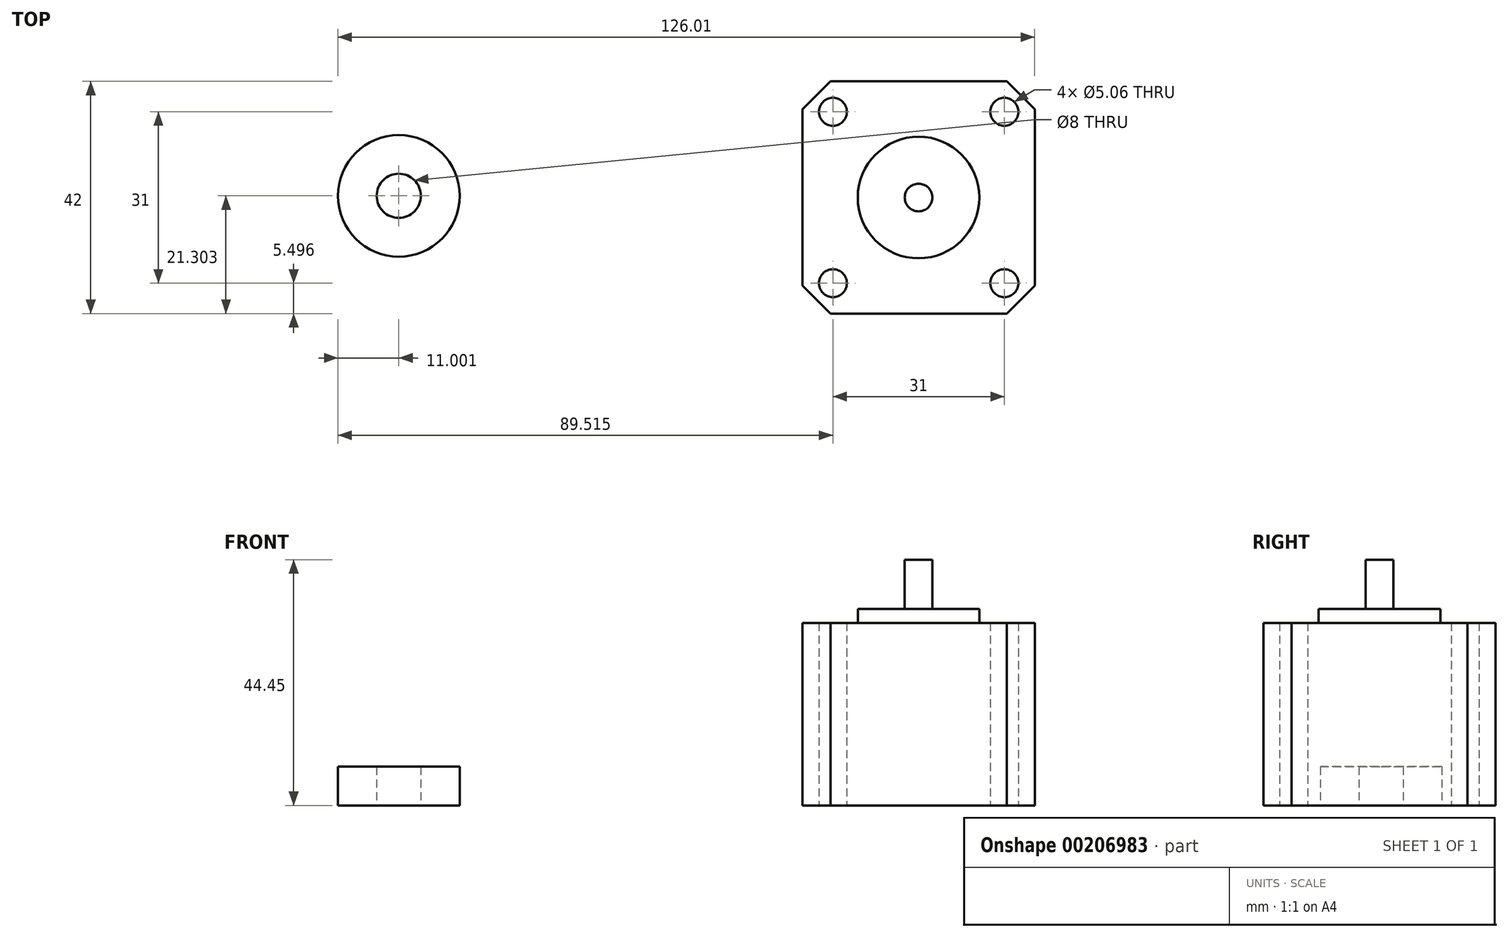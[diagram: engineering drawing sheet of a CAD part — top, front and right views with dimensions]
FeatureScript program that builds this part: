
annotation { "Feature Type Name" : "Feature", "Feature Type Description" : "" }
export const myFeature = defineFeature(function(context is Context, id is Id, definition is map)
    precondition{}
    {
        {
            var Q0;
            Q0=qCreatedBy(makeId("Top.planeOp"),FACE);
            var sketch = newSketch(context, id + "F0", { "sketchPlane" : qUnion([Q0])});
            skCircle(sketch, "E0", {"center": v(-49.86, 22.61) * mm, "radius": 11 * mm});
            skCircle(sketch, "E1", {"center": v(-49.86, 22.61) * mm, "radius": 4 * mm});
            skSolve(sketch);
        }
        {
            var Q0;
            Q0 = qSketchRegion(id + "F0", true);
            extrude(context, id + "F1", {"entities" : qUnion([Q0]), "depth" : 7 * mm});
        }
        {
            var Q0;
            Q0=qCreatedBy(makeId("Top.planeOp"),FACE);
            var sketch = newSketch(context, id + "F2", { "sketchPlane" : qUnion([Q0])});
            skLineSegment(sketch, "E2.bottom", {"start": v(23.15, 43.3) * mm, "end": v(65.15, 43.3) * mm});
            skLineSegment(sketch, "E2.top", {"start": v(23.15, 1.3) * mm, "end": v(65.15, 1.3) * mm});
            skLineSegment(sketch, "E2.left", {"start": v(23.15, 43.3) * mm, "end": v(23.15, 1.3) * mm});
            skLineSegment(sketch, "E2.right", {"start": v(65.15, 43.3) * mm, "end": v(65.15, 1.3) * mm});
            skCircle(sketch, "E3", {"center": v(44.15, 22.3) * mm, "radius": 11 * mm});
            skPoint(sketch, "E3.centerSnap0", {"position": v(23.15, 22.3) * mm});
            skPoint(sketch, "E3.centerSnap1", {"position": v(44.15, 43.3) * mm});
            skCircle(sketch, "E4", {"center": v(44.15, 22.3) * mm, "radius": 2.5 * mm});
            skCircle(sketch, "E5", {"center": v(28.65, 37.8) * mm, "radius": 2.53 * mm});
            skCircle(sketch, "E6", {"center": v(28.65, 6.8) * mm, "radius": 2.53 * mm});
            skCircle(sketch, "E7", {"center": v(59.65, 6.8) * mm, "radius": 2.53 * mm});
            skCircle(sketch, "E8", {"center": v(59.65, 37.8) * mm, "radius": 2.53 * mm});
            skLineSegment(sketch, "E9.bottom", {"start": v(28.65, 37.8) * mm, "end": v(59.65, 37.8) * mm, "construction": true});
            skLineSegment(sketch, "E9.top", {"start": v(28.65, 6.8) * mm, "end": v(59.65, 6.8) * mm, "construction": true});
            skLineSegment(sketch, "E9.left", {"start": v(28.65, 37.8) * mm, "end": v(28.65, 6.8) * mm, "construction": true});
            skLineSegment(sketch, "E9.right", {"start": v(59.65, 37.8) * mm, "end": v(59.65, 6.8) * mm, "construction": true});
            skLineSegment(sketch, "E10", {"start": v(28.65, 37.8) * mm, "end": v(28.65, 43.3) * mm, "construction": true});
            skLineSegment(sketch, "E11", {"start": v(28.65, 37.8) * mm, "end": v(23.15, 37.8) * mm, "construction": true});
            skLineSegment(sketch, "E12", {"start": v(59.65, 6.8) * mm, "end": v(65.15, 6.8) * mm, "construction": true});
            skSolve(sketch);
        }
        {
            var Q0;
            Q0=makeQuery(id+"F2.imprint","IMPRINT",FACE,{"disambiguationData":[TD([[makeQuery(id+"F2.imprint","IMPRINT",EDGE,{"derivedFrom":sQuery(id+"F2.wireOp",EDGE,"E2.bottom")}),-1.0]])]});
            extrude(context, id + "F3", {"entities" : qUnion([Q0]), "depth" : 33.02 * mm});
        }
        {
            var Q0;
            Q0=makeQuery(id+"F2.imprint","IMPRINT",FACE,{"disambiguationData":[TD([[makeQuery(id+"F2.imprint","IMPRINT",EDGE,{"derivedFrom":sQuery(id+"F2.wireOp",EDGE,"E3")}),1.0]])]});
            extrude(context, id + "F4", {"entities" : qUnion([Q0]), "operationType" : NewBodyOperationType.ADD, "depth" : 35.56 * mm});
        }
        {
            var Q0;
            Q0=makeQuery(id+"F2.imprint","IMPRINT",FACE,{"disambiguationData":[TD([[makeQuery(id+"F2.imprint","IMPRINT",EDGE,{"derivedFrom":sQuery(id+"F2.wireOp",EDGE,"E4")}),1.0]])]});
            extrude(context, id + "F5", {"entities" : qUnion([Q0]), "operationType" : NewBodyOperationType.ADD, "depth" : 44.45 * mm});
        }
        {
            var Q0;
            Q0=makeQuery(id+"F3.opExtrude","SWEPT_EDGE",EDGE,{"disambiguationData":[OSD([sQuery(id+"F2.wireOp",EDGE,"E2.bottom"),sQuery(id+"F2.wireOp",EDGE,"E2.left")])]});
            var Q1;
            Q1=makeQuery(id+"F3.opExtrude","SWEPT_EDGE",EDGE,{"disambiguationData":[OSD([sQuery(id+"F2.wireOp",EDGE,"E2.top"),sQuery(id+"F2.wireOp",EDGE,"E2.left")])]});
            var Q2;
            Q2=makeQuery(id+"F3.opExtrude","SWEPT_EDGE",EDGE,{"disambiguationData":[OSD([sQuery(id+"F2.wireOp",EDGE,"E2.top"),sQuery(id+"F2.wireOp",EDGE,"E2.right")])]});
            var Q3;
            Q3=makeQuery(id+"F3.opExtrude","SWEPT_EDGE",EDGE,{"disambiguationData":[OSD([sQuery(id+"F2.wireOp",EDGE,"E2.bottom"),sQuery(id+"F2.wireOp",EDGE,"E2.right")])]});
            chamfer(context, id + "F6", {"entities" : qUnion([Q0, Q1, Q2, Q3]), "width" : 5.08 * mm, "tangentPropagation" : true});
        }
    });
